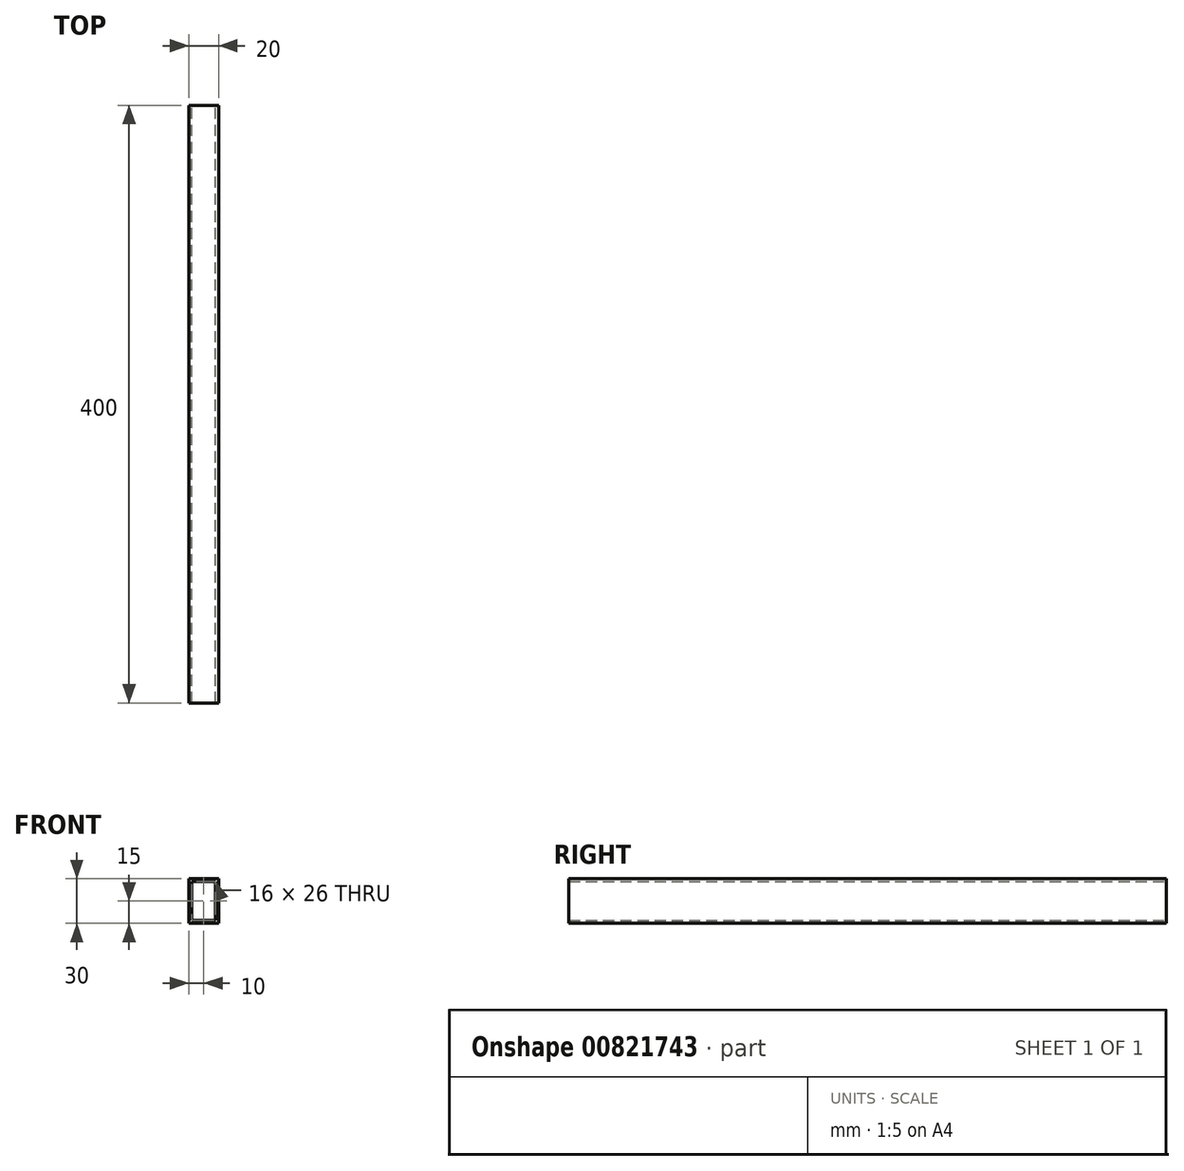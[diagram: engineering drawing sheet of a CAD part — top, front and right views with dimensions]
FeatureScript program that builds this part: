
annotation { "Feature Type Name" : "Feature", "Feature Type Description" : "" }
export const myFeature = defineFeature(function(context is Context, id is Id, definition is map)
    precondition{}
    {
        {
            var Q0;
            Q0=qCreatedBy(makeId("Front.planeOp"),FACE);
            var sketch = newSketch(context, id + "F0", { "sketchPlane" : qUnion([Q0])});
            skLineSegment(sketch, "E0.bottom", {"start": v(10, 15) * mm, "end": v(-10, 15) * mm});
            skLineSegment(sketch, "E0.top", {"start": v(10, -15) * mm, "end": v(-10, -15) * mm});
            skLineSegment(sketch, "E0.left", {"start": v(10, 15) * mm, "end": v(10, -15) * mm});
            skLineSegment(sketch, "E0.right", {"start": v(-10, 15) * mm, "end": v(-10, -15) * mm});
            skPoint(sketch, "E0.middle", {"position": v(0, 0) * mm});
            skLineSegment(sketch, "E1.0", {"start": v(8, 13) * mm, "end": v(-8, 13) * mm});
            skLineSegment(sketch, "E1.1", {"start": v(8, 13) * mm, "end": v(8, -13) * mm});
            skLineSegment(sketch, "E1.2", {"start": v(8, -13) * mm, "end": v(-8, -13) * mm});
            skLineSegment(sketch, "E1.3", {"start": v(-8, 13) * mm, "end": v(-8, -13) * mm});
            skSolve(sketch);
        }
        {
            var Q0;
            Q0 = qSketchRegion(id + "F0", true);
            extrude(context, id + "F1", {"entities" : qUnion([Q0]), "depth" : 400 * mm, "offsetDistance" : 25 * mm});
        }
    });
